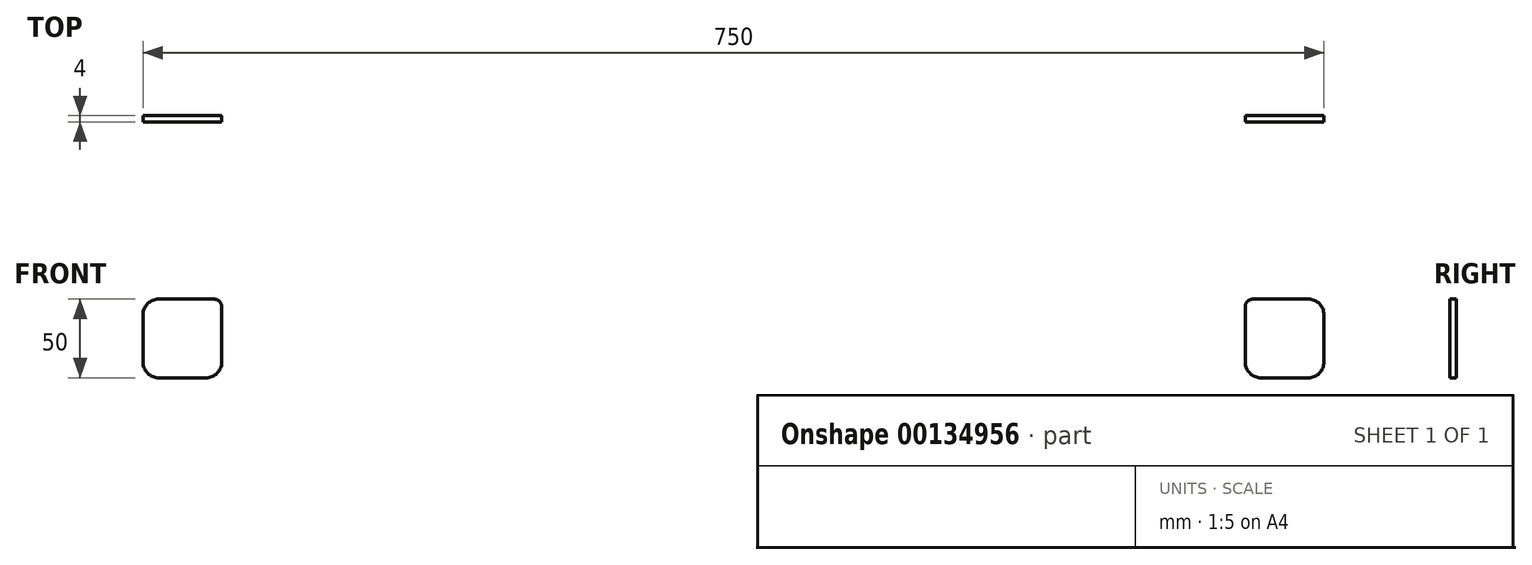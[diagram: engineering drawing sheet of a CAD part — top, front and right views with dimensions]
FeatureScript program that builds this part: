
annotation { "Feature Type Name" : "Feature", "Feature Type Description" : "" }
export const myFeature = defineFeature(function(context is Context, id is Id, definition is map)
    precondition{}
    {
        {
            var Q0;
            Q0=qCreatedBy(makeId("Front.planeOp"),FACE);
            var sketch = newSketch(context, id + "F0", { "sketchPlane" : qUnion([Q0])});
            skLineSegment(sketch, "E0.bottom", {"start": v(0, 0) * mm, "end": v(750, 0) * mm});
            skLineSegment(sketch, "E0.top", {"start": v(0, 406.37) * mm, "end": v(750, 406.37) * mm});
            skLineSegment(sketch, "E0.left", {"start": v(0, 0) * mm, "end": v(0, 406.37) * mm});
            skLineSegment(sketch, "E0.right", {"start": v(750, 0) * mm, "end": v(750, 406.37) * mm});
            skLineSegment(sketch, "E1.bottom", {"start": v(0, 0) * mm, "end": v(50, 0) * mm});
            skLineSegment(sketch, "E1.top", {"start": v(0, 50) * mm, "end": v(50, 50) * mm});
            skLineSegment(sketch, "E1.left", {"start": v(0, 0) * mm, "end": v(0, 50) * mm});
            skLineSegment(sketch, "E1.right", {"start": v(50, 0) * mm, "end": v(50, 50) * mm});
            skLineSegment(sketch, "E2.bottom", {"start": v(0, 406.37) * mm, "end": v(50, 406.37) * mm});
            skLineSegment(sketch, "E2.top", {"start": v(0, 356.37) * mm, "end": v(50, 356.37) * mm});
            skLineSegment(sketch, "E2.left", {"start": v(0, 406.37) * mm, "end": v(0, 356.37) * mm});
            skLineSegment(sketch, "E2.right", {"start": v(50, 406.37) * mm, "end": v(50, 356.37) * mm});
            skLineSegment(sketch, "E3.bottom", {"start": v(750, 406.37) * mm, "end": v(700, 406.37) * mm});
            skLineSegment(sketch, "E3.top", {"start": v(750, 356.37) * mm, "end": v(700, 356.37) * mm});
            skLineSegment(sketch, "E3.left", {"start": v(750, 406.37) * mm, "end": v(750, 356.37) * mm});
            skLineSegment(sketch, "E3.right", {"start": v(700, 406.37) * mm, "end": v(700, 356.37) * mm});
            skLineSegment(sketch, "E4.bottom", {"start": v(750, 0) * mm, "end": v(700, 0) * mm});
            skLineSegment(sketch, "E4.top", {"start": v(750, 50) * mm, "end": v(700, 50) * mm});
            skLineSegment(sketch, "E4.left", {"start": v(750, 0) * mm, "end": v(750, 50) * mm});
            skLineSegment(sketch, "E4.right", {"start": v(700, 0) * mm, "end": v(700, 50) * mm});
            skLineSegment(sketch, "E5", {"start": v(37.5, 50) * mm, "end": v(37.5, 62.5) * mm});
            skLineSegment(sketch, "E6", {"start": v(712.5, 50) * mm, "end": v(712.5, 62.5) * mm});
            skLineSegment(sketch, "E7", {"start": v(712.5, 356.37) * mm, "end": v(712.5, 343.87) * mm});
            skLineSegment(sketch, "E8", {"start": v(37.5, 356.37) * mm, "end": v(37.5, 343.87) * mm});
            skCircle(sketch, "E9", {"center": v(37.5, 343.87) * mm, "radius": 3.25 * mm});
            skCircle(sketch, "E10", {"center": v(37.5, 62.5) * mm, "radius": 3.25 * mm});
            skCircle(sketch, "E11", {"center": v(712.5, 62.5) * mm, "radius": 3.25 * mm});
            skCircle(sketch, "E12", {"center": v(712.5, 343.87) * mm, "radius": 3.25 * mm});
            skSolve(sketch);
        }
        {
            var Q0;
            Q0=makeQuery(id+"F0.imprint","IMPRINT",FACE,{"disambiguationData":[TD([[makeQuery(id+"F0.imprint","IMPRINT",EDGE,{"derivedFrom":sQuery(id+"F0.wireOp",EDGE,"E0.bottom")}),1.0]])]});
            extrude(context, id + "F1", {"entities" : qUnion([Q0]), "depth" : 4 * mm});
        }
        {
            var Q0;
            Q0=makeQuery(id+"F1.opExtrude","SWEPT_EDGE",EDGE,{"disambiguationData":[OSD([sQuery(id+"F0.wireOp",EDGE,"E0.left"),sQuery(id+"F0.wireOp",EDGE,"E2.top"),sQuery(id+"F0.wireOp",EDGE,"E2.left")])]});
            var Q1;
            Q1=makeQuery(id+"F1.opExtrude","SWEPT_EDGE",EDGE,{"disambiguationData":[OSD([sQuery(id+"F0.wireOp",EDGE,"E0.top"),sQuery(id+"F0.wireOp",EDGE,"E2.bottom"),sQuery(id+"F0.wireOp",EDGE,"E2.right")])]});
            var Q2;
            Q2=makeQuery(id+"F1.opExtrude","SWEPT_EDGE",EDGE,{"disambiguationData":[OSD([sQuery(id+"F0.wireOp",EDGE,"E0.left"),sQuery(id+"F0.wireOp",EDGE,"E1.top"),sQuery(id+"F0.wireOp",EDGE,"E1.left")])]});
            var Q3;
            Q3=makeQuery(id+"F1.opExtrude","SWEPT_EDGE",EDGE,{"disambiguationData":[OSD([sQuery(id+"F0.wireOp",EDGE,"E0.bottom"),sQuery(id+"F0.wireOp",EDGE,"E1.bottom"),sQuery(id+"F0.wireOp",EDGE,"E1.right")])]});
            var Q4;
            Q4=makeQuery(id+"F1.opExtrude","SWEPT_EDGE",EDGE,{"disambiguationData":[OSD([sQuery(id+"F0.wireOp",EDGE,"E0.bottom"),sQuery(id+"F0.wireOp",EDGE,"E4.bottom"),sQuery(id+"F0.wireOp",EDGE,"E4.right")])]});
            var Q5;
            Q5=makeQuery(id+"F1.opExtrude","SWEPT_EDGE",EDGE,{"disambiguationData":[OSD([sQuery(id+"F0.wireOp",EDGE,"E0.right"),sQuery(id+"F0.wireOp",EDGE,"E4.top"),sQuery(id+"F0.wireOp",EDGE,"E4.left")])]});
            var Q6;
            Q6=makeQuery(id+"F1.opExtrude","SWEPT_EDGE",EDGE,{"disambiguationData":[OSD([sQuery(id+"F0.wireOp",EDGE,"E0.right"),sQuery(id+"F0.wireOp",EDGE,"E3.top"),sQuery(id+"F0.wireOp",EDGE,"E3.left")])]});
            var Q7;
            Q7=makeQuery(id+"F1.opExtrude","SWEPT_EDGE",EDGE,{"disambiguationData":[OSD([sQuery(id+"F0.wireOp",EDGE,"E0.top"),sQuery(id+"F0.wireOp",EDGE,"E3.bottom"),sQuery(id+"F0.wireOp",EDGE,"E3.right")])]});
            fillet(context, id + "F2", {"entities" : qUnion([Q0, Q1, Q2, Q3, Q4, Q5, Q6, Q7]), "radius" : 10 * mm, "tangentPropagation" : true, "allowEdgeOverflow" : false});
        }
        {
            var Q0;
            Q0=makeQuery(id+"F1.opExtrude","SWEPT_EDGE",EDGE,{"disambiguationData":[OSD([sQuery(id+"F0.wireOp",EDGE,"E3.top"),sQuery(id+"F0.wireOp",EDGE,"E3.right")])]});
            var Q1;
            Q1=makeQuery(id+"F1.opExtrude","SWEPT_EDGE",EDGE,{"disambiguationData":[OSD([sQuery(id+"F0.wireOp",EDGE,"E4.top"),sQuery(id+"F0.wireOp",EDGE,"E4.right")])]});
            var Q2;
            Q2=makeQuery(id+"F1.opExtrude","SWEPT_EDGE",EDGE,{"disambiguationData":[OSD([sQuery(id+"F0.wireOp",EDGE,"E1.top"),sQuery(id+"F0.wireOp",EDGE,"E1.right")])]});
            var Q3;
            Q3=makeQuery(id+"F1.opExtrude","SWEPT_EDGE",EDGE,{"disambiguationData":[OSD([sQuery(id+"F0.wireOp",EDGE,"E2.top"),sQuery(id+"F0.wireOp",EDGE,"E2.right")])]});
            fillet(context, id + "F3", {"entities" : qUnion([Q0, Q1, Q2, Q3]), "radius" : 5 * mm, "tangentPropagation" : true, "allowEdgeOverflow" : false});
        }
    });
